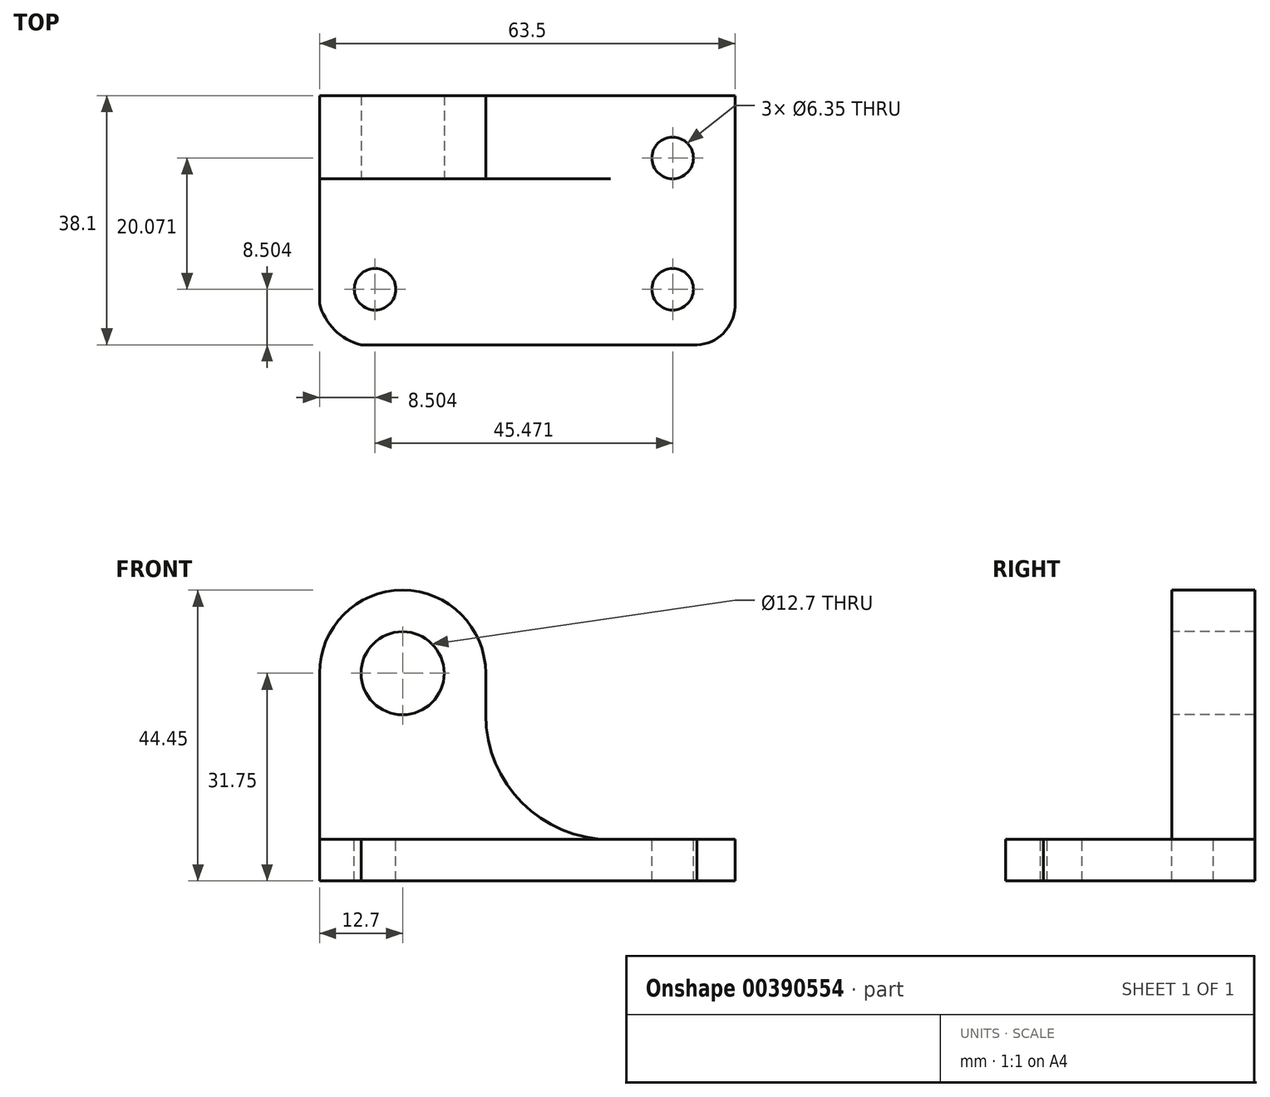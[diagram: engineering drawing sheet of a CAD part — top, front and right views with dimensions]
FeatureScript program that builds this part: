
annotation { "Feature Type Name" : "Feature", "Feature Type Description" : "" }
export const myFeature = defineFeature(function(context is Context, id is Id, definition is map)
    precondition{}
    {
        {
            var Q0;
            Q0=qCreatedBy(makeId("Top.planeOp"),FACE);
            var sketch = newSketch(context, id + "F0", { "sketchPlane" : qUnion([Q0])});
            skLineSegment(sketch, "E0", {"start": v(0, 0) * mm, "end": v(63.5, 0) * mm});
            skLineSegment(sketch, "E1", {"start": v(63.5, 0) * mm, "end": v(63.5, 38.1) * mm});
            skLineSegment(sketch, "E2", {"start": v(63.5, 38.1) * mm, "end": v(0, 38.1) * mm});
            skLineSegment(sketch, "E3", {"start": v(0, 38.1) * mm, "end": v(0, 0) * mm});
            skSolve(sketch);
        }
        {
            var Q0;
            Q0 = qSketchRegion(id + "F0", true);
            extrude(context, id + "F1", {"entities" : qUnion([Q0]), "depth" : 6.35 * mm});
        }
        {
            var Q0;
            Q0=makeQuery(id+"F1.opExtrude","CAP_FACE",FACE,{"disambiguationData":[OSD([sQuery(id+"F0.wireOp",EDGE,"E0"),sQuery(id+"F0.wireOp",EDGE,"E1"),sQuery(id+"F0.wireOp",EDGE,"E2"),sQuery(id+"F0.wireOp",EDGE,"E3")])],"isStart":false});
            var sketch = newSketch(context, id + "F2", { "sketchPlane" : qUnion([Q0])});
            skLineSegment(sketch, "E4", {"start": v(0, 25.4) * mm, "end": v(44.45, 25.4) * mm});
            skLineSegment(sketch, "E5", {"start": v(44.45, 25.4) * mm, "end": v(44.45, 38.1) * mm});
            skSolve(sketch);
        }
        {
            var Q0;
            Q0 = qSketchRegion(id + "F2", true);
            var Q1;
            {var subQ0=sQuery(id+"F2.wireOp",EDGE,"E4");Q1=makeQuery(id+"F2.imprint","IMPRINT",FACE,{"disambiguationData":[TD([[makeQuery(id+"F2.imprint","IMPRINT",EDGE,{"derivedFrom":subQ0}),1.0]])]});}
            extrude(context, id + "F3", {"entities" : qUnion([Q0, Q1]), "operationType" : NewBodyOperationType.ADD, "depth" : 38.1 * mm});
        }
        {
            var Q0;
            Q0=makeQuery(id+"F3.opExtrude","SWEPT_FACE",FACE,{"disambiguationData":[OSD([sQuery(id+"F2.wireOp",EDGE,"E4")])]});
            var sketch = newSketch(context, id + "F4", { "sketchPlane" : qUnion([Q0])});
            skCircle(sketch, "E6", {"center": v(12.7, 31.75) * mm, "radius": 6.35 * mm});
            skSolve(sketch);
        }
        {
            var Q0;
            Q0=makeQuery(id+"F4.imprint","IMPRINT",FACE,{"disambiguationData":[TD([[makeQuery(id+"F4.imprint","IMPRINT",EDGE,{"derivedFrom":sQuery(id+"F4.wireOp",EDGE,"E6")}),1.0]])]});
            extrude(context, id + "F5", {"entities" : qUnion([Q0]), "operationType" : NewBodyOperationType.REMOVE, "oppositeDirection" : true, "depth" : 25.4 * mm});
        }
        {
            var Q0;
            Q0=makeQuery(id+"F3.opExtrude","SWEPT_FACE",FACE,{"disambiguationData":[OSD([sQuery(id+"F2.wireOp",EDGE,"E4")])]});
            var sketch = newSketch(context, id + "F6", { "sketchPlane" : qUnion([Q0])});
            skCircle(sketch, "E7", {"center": v(12.7, 31.75) * mm, "radius": 12.7 * mm});
            skPoint(sketch, "E8.endSnap0", {"position": v(44.45, 25.4) * mm});
            skLineSegment(sketch, "E9", {"start": v(25.4, 31.75) * mm, "end": v(25.4, 26.15) * mm});
            skArc(sketch, "E10", {"start": v(25.4, 26.15) * mm, "mid": v(30.71, 12.2) * mm, "end": v(44.45, 6.35) * mm});
            skSolve(sketch);
        }
        {
            var Q0;
            {var subQ0=sQuery(id+"F6.wireOp",EDGE,"E7");var subQ1=sQuery(id+"F2.wireOp",EDGE,"E4");var subQ4=makeQuery(id+"F3.opExtrude","CAP_EDGE",EDGE,{"disambiguationData":[OSD([subQ1])],"isStart":false});var subQ5=makeQuery(id+"F6.imprint","INTERSECT",VERTEX,{"derivedFrom":[subQ4,subQ0]});Q0=makeQuery(id+"F6.imprint","IMPRINT",FACE,{"disambiguationData":[TD([[makeQuery(id+"F6.imprint","IMPRINT",EDGE,{"disambiguationData":[TD([[subQ5,-1.0]])],"derivedFrom":subQ0}),-1.0]])]});}
            var Q1;
            {var subQ0=sQuery(id+"F6.wireOp",EDGE,"H9yuP0xS-eGCV-P7lX-5pBX-46697FAsPeL6");Q1=makeQuery(id+"F6.imprint","IMPRINT",FACE,{"disambiguationData":[TD([[makeQuery(id+"F6.imprint","IMPRINT",EDGE,{"derivedFrom":subQ0}),1.0]])]});}
            extrude(context, id + "F7", {"entities" : qUnion([Q0, Q1]), "operationType" : NewBodyOperationType.REMOVE, "oppositeDirection" : true, "depth" : 25.4 * mm});
        }
        {
            var Q0;
            Q0=makeQuery(id+"F3.opExtrude","SWEPT_FACE",FACE,{"disambiguationData":[OSD([sQuery(id+"F2.wireOp",EDGE,"E4")])]});
            var sketch = newSketch(context, id + "F8", { "sketchPlane" : qUnion([Q0])});
            skCircle(sketch, "E11", {"center": v(12.7, 31.75) * mm, "radius": 12.7 * mm});
            skLineSegment(sketch, "E12", {"start": v(25.4, 31.75) * mm, "end": v(25.4, 25.4) * mm});
            skPoint(sketch, "E12.endSnap0", {"position": v(44.45, 25.4) * mm});
            skArc(sketch, "E13", {"start": v(25.4, 25.4) * mm, "mid": v(30.98, 11.93) * mm, "end": v(44.45, 6.35) * mm});
            skSolve(sketch);
        }
        {
            var Q0;
            Q0=makeQuery(id+"F1.opExtrude","CAP_FACE",FACE,{"disambiguationData":[OSD([sQuery(id+"F0.wireOp",EDGE,"E0"),sQuery(id+"F0.wireOp",EDGE,"E1"),sQuery(id+"F0.wireOp",EDGE,"E2"),sQuery(id+"F0.wireOp",EDGE,"E3")])],"isStart":false});
            var sketch = newSketch(context, id + "F9", { "sketchPlane" : qUnion([Q0])});
            skArc(sketch, "E14", {"start": v(0, 6.35) * mm, "mid": v(2.3, 2.3) * mm, "end": v(6.35, 0) * mm});
            skSolve(sketch);
        }
        {
            var Q0;
            Q0 = qSketchRegion(id + "F9", true);
            var Q1;
            {var subQ0=sQuery(id+"F9.wireOp",EDGE,"E14");Q1=makeQuery(id+"F9.imprint","IMPRINT",FACE,{"disambiguationData":[TD([[makeQuery(id+"F9.imprint","IMPRINT",EDGE,{"derivedFrom":subQ0}),-1.0]])]});}
            extrude(context, id + "F10", {"entities" : qUnion([Q0, Q1]), "operationType" : NewBodyOperationType.REMOVE, "oppositeDirection" : true, "depth" : 25.4 * mm});
        }
        {
            var Q0;
            Q0=makeQuery(id+"F1.opExtrude","CAP_FACE",FACE,{"disambiguationData":[OSD([sQuery(id+"F0.wireOp",EDGE,"E0"),sQuery(id+"F0.wireOp",EDGE,"E1"),sQuery(id+"F0.wireOp",EDGE,"E2"),sQuery(id+"F0.wireOp",EDGE,"E3")])],"isStart":false});
            var sketch = newSketch(context, id + "F11", { "sketchPlane" : qUnion([Q0])});
            skArc(sketch, "E15", {"start": v(57.15, 0) * mm, "mid": v(61.72, 1.78) * mm, "end": v(63.5, 6.35) * mm});
            skSolve(sketch);
        }
        {
            var Q0;
            Q0 = qSketchRegion(id + "F11", true);
            var Q1;
            {var subQ0=sQuery(id+"F11.wireOp",EDGE,"E15");var subQ1=makeQuery(id+"F1.opExtrude","CAP_EDGE",EDGE,{"disambiguationData":[OSD([sQuery(id+"F0.wireOp",EDGE,"E0")])],"isStart":false});var subQ2=makeQuery(id+"F11.imprint","INTERSECT",VERTEX,{"disambiguationData":[OD(1.0)],"derivedFrom":[subQ1,subQ0]});Q1=makeQuery(id+"F11.imprint","IMPRINT",FACE,{"disambiguationData":[TD([[makeQuery(id+"F11.imprint","IMPRINT",EDGE,{"disambiguationData":[TD([[subQ2,-1.0]])],"derivedFrom":subQ0}),-1.0]])]});}
            extrude(context, id + "F12", {"entities" : qUnion([Q0, Q1]), "operationType" : NewBodyOperationType.REMOVE, "oppositeDirection" : true, "depth" : 25.4 * mm});
        }
        {
            var Q0;
            Q0=makeQuery(id+"F1.opExtrude","CAP_FACE",FACE,{"disambiguationData":[OSD([sQuery(id+"F0.wireOp",EDGE,"E0"),sQuery(id+"F0.wireOp",EDGE,"E1"),sQuery(id+"F0.wireOp",EDGE,"E2"),sQuery(id+"F0.wireOp",EDGE,"E3")])],"isStart":false});
            var sketch = newSketch(context, id + "F13", { "sketchPlane" : qUnion([Q0])});
            skCircle(sketch, "E16", {"center": v(8.5, 8.5) * mm, "radius": 3.18 * mm});
            skCircle(sketch, "E17", {"center": v(53.97, 8.5) * mm, "radius": 3.18 * mm});
            skCircle(sketch, "E18", {"center": v(53.98, 28.58) * mm, "radius": 3.18 * mm});
            skSolve(sketch);
        }
        {
            var Q0;
            Q0=makeQuery(id+"F13.imprint","IMPRINT",FACE,{"disambiguationData":[TD([[makeQuery(id+"F13.imprint","IMPRINT",EDGE,{"derivedFrom":sQuery(id+"F13.wireOp",EDGE,"E18")}),1.0]])]});
            var Q1;
            Q1=makeQuery(id+"F13.imprint","IMPRINT",FACE,{"disambiguationData":[TD([[makeQuery(id+"F13.imprint","IMPRINT",EDGE,{"derivedFrom":sQuery(id+"F13.wireOp",EDGE,"E17")}),1.0]])]});
            var Q2;
            Q2=makeQuery(id+"F13.imprint","IMPRINT",FACE,{"disambiguationData":[TD([[makeQuery(id+"F13.imprint","IMPRINT",EDGE,{"derivedFrom":sQuery(id+"F13.wireOp",EDGE,"E16")}),1.0]])]});
            extrude(context, id + "F14", {"entities" : qUnion([Q0, Q1, Q2]), "operationType" : NewBodyOperationType.REMOVE, "oppositeDirection" : true, "depth" : 25.4 * mm});
        }
        {
            var Q0;
            {var subQ0=sQuery(id+"F8.wireOp",EDGE,"E12");Q0=makeQuery(id+"F8.imprint","IMPRINT",FACE,{"disambiguationData":[TD([[makeQuery(id+"F8.imprint","IMPRINT",EDGE,{"derivedFrom":subQ0}),1.0]])]});}
            extrude(context, id + "F15", {"entities" : qUnion([Q0]), "operationType" : NewBodyOperationType.REMOVE, "oppositeDirection" : true, "depth" : 25.4 * mm});
        }
    });
